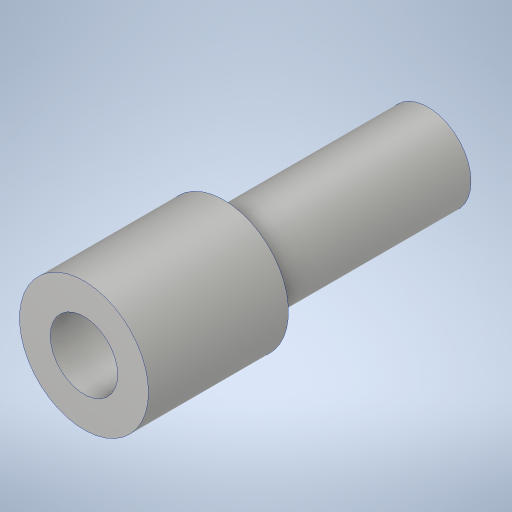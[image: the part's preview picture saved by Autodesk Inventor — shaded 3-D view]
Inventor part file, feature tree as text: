
AUTODESK INVENTOR PART (.ipt)
format: ipt  version: 2023.4 (Build 274418000, 418)  size: 248,320 bytes
history: native  units: in
note: dims shown in document units (in); Inventor stores cm internally (conversion verified against a paired STEP export)
features: sketch x3, extrude x2, hole x1, projected_geometry x1
ambient origin geometry x8: Origin, YZ Plane, XZ Plane, XY Plane, X Axis, Y Axis, Z Axis, Center Point
bodies: Solid1 (feature_tree)
feature tree (7):
  extrude  "Extrusion1"  Depth=1.0in TaperAngle=0.0deg
  hole  "Hole1"  [1 undecoded]
  extrude  "Extrusion2"  [1 undecoded]
  sketch  "Sketch1"  dims[d0=0.375in d1=1.0in d2=0.0in]
  sketch  "Sketch3"  dims[d3=0.196in d4=0.38in d5=0.385in d6=0.25in d7=0.5635in d8=0.536in d9=0.8108in d10=0.25in]
  sketch  "Sketch4"  dims[d11=0.593in d12=0.0in]
  projected_geometry  "Projected Loop1"
note: 2 required parameter values undecoded (feature->parameter linkage not recoverable at this tier; creation-order binding heuristic only, values carry confidence <= 0.55)
